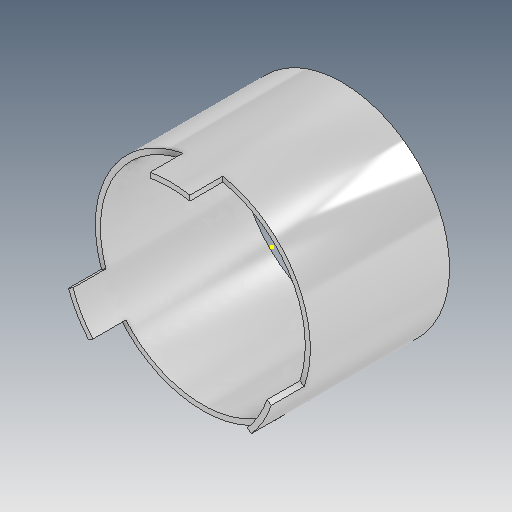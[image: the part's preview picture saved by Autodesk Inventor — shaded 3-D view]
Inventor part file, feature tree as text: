
AUTODESK INVENTOR PART (.ipt)
format: ipt  version: 2020.3 (Build 243373010, 373A)  size: 168,448 bytes
history: native  units: mm
features: sketch x3, extrude x2, pattern_circular x1, plane x1
ambient origin geometry x8: Origin, YZ Plane, XZ Plane, XY Plane, X Axis, Y Axis, Z Axis, Center Point
bodies: Solid1 (feature_tree)
feature tree (7):
  extrude  "Extrusion1"  Depth=1.0mm
  extrude  "Extrusion2"  Depth=7.85mm
  pattern_circular  "Circular Pattern1"  Count=3 Angle=360.0deg
  sketch  "Sketch3"  dims[d5=6.5mm d6=0.0mm d7=30.0mm d8=360.0deg d10=20.25mm]
  plane  "Work Plane1"
  sketch  "Sketch1"  dims[d0=42.475mm d1=1.0mm]
  sketch  "Sketch2"  dims[d2=27.5mm d3=0.0mm d4=7.85mm]
